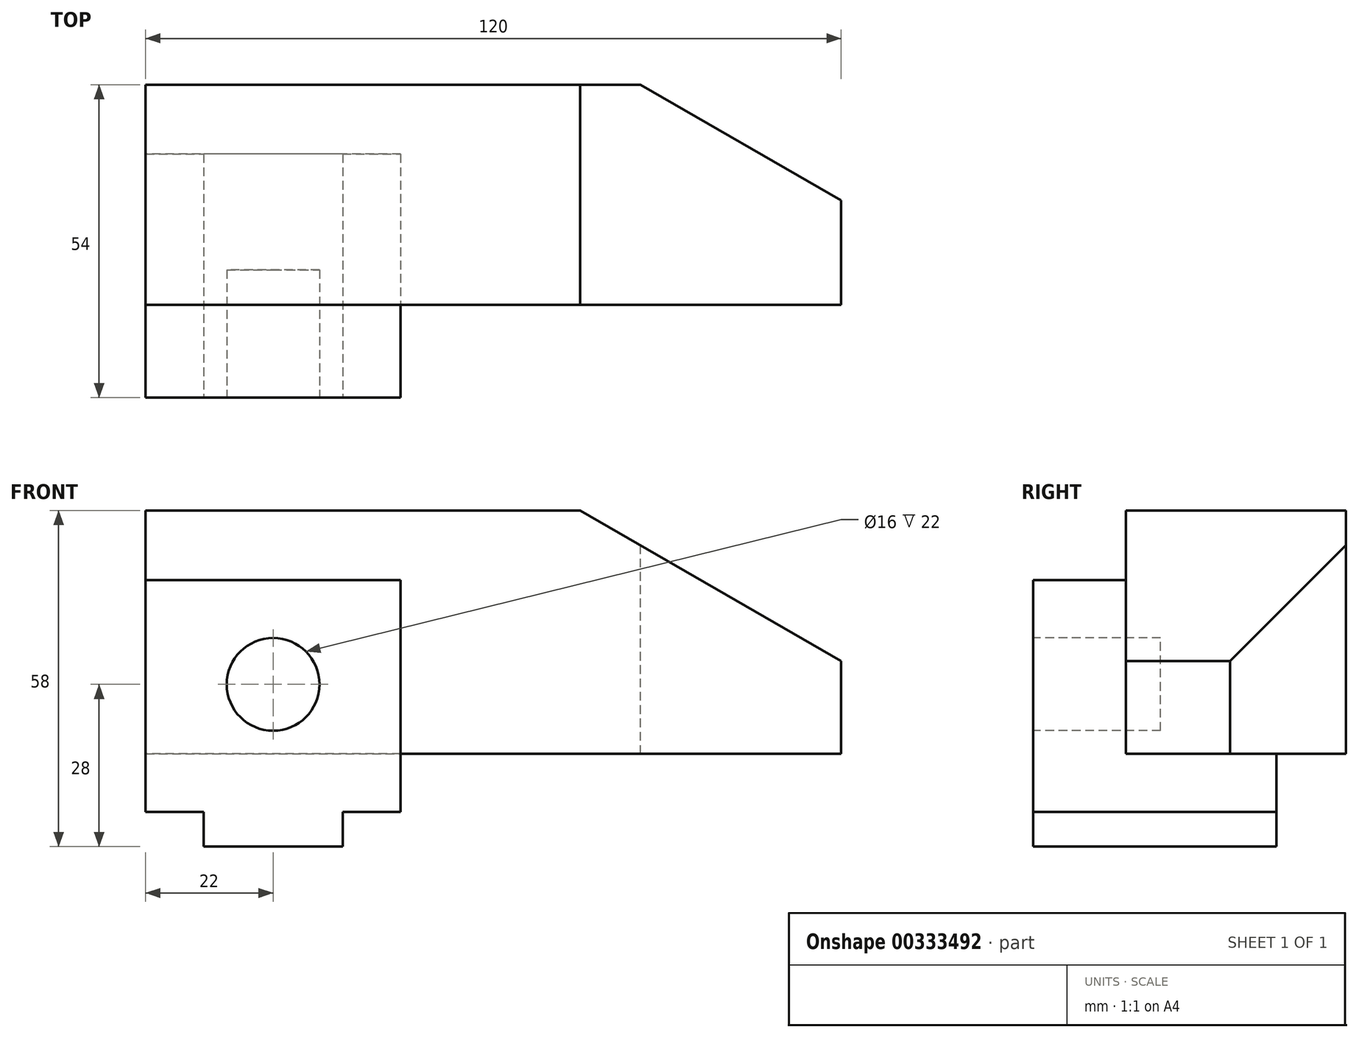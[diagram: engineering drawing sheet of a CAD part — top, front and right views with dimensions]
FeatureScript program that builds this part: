
annotation { "Feature Type Name" : "Feature", "Feature Type Description" : "" }
export const myFeature = defineFeature(function(context is Context, id is Id, definition is map)
    precondition{}
    {
        {
            var Q0;
            Q0=qCreatedBy(makeId("Front.planeOp"),FACE);
            var sketch = newSketch(context, id + "F0", { "sketchPlane" : qUnion([Q0])});
            skLineSegment(sketch, "E0.bottom", {"start": v(0, 0) * mm, "end": v(120, 0) * mm});
            skLineSegment(sketch, "E0.top", {"start": v(0, 58) * mm, "end": v(120, 58) * mm});
            skLineSegment(sketch, "E0.left", {"start": v(0, 0) * mm, "end": v(0, 58) * mm});
            skLineSegment(sketch, "E0.right", {"start": v(120, 0) * mm, "end": v(120, 58) * mm});
            skSolve(sketch);
        }
        {
            var Q0;
            Q0 = qSketchRegion(id + "F0", true);
            extrude(context, id + "F1", {"entities" : qUnion([Q0]), "depth" : 54 * mm});
        }
        {
            var Q0;
            Q0=makeQuery(id+"F1.opExtrude","CAP_FACE",FACE,{"disambiguationData":[OSD([sQuery(id+"F0.wireOp",EDGE,"E0.bottom"),sQuery(id+"F0.wireOp",EDGE,"E0.top"),sQuery(id+"F0.wireOp",EDGE,"E0.left"),sQuery(id+"F0.wireOp",EDGE,"E0.right")])],"isStart":false});
            var sketch = newSketch(context, id + "F2", { "sketchPlane" : qUnion([Q0])});
            skLineSegment(sketch, "E1", {"start": v(34, 0) * mm, "end": v(34, 6) * mm});
            skLineSegment(sketch, "E2", {"start": v(34, 6) * mm, "end": v(44, 6) * mm});
            skLineSegment(sketch, "E3", {"start": v(44, 6) * mm, "end": v(44, 16) * mm});
            skLineSegment(sketch, "E4", {"start": v(44, 16) * mm, "end": v(120, 16) * mm});
            skLineSegment(sketch, "E5", {"start": v(120, 16) * mm, "end": v(120, 0) * mm});
            skLineSegment(sketch, "E6", {"start": v(120, 0) * mm, "end": v(34, 0) * mm});
            skLineSegment(sketch, "E7", {"start": v(75, 58) * mm, "end": v(120, 32.02) * mm});
            skLineSegment(sketch, "E8", {"start": v(120, 32.02) * mm, "end": v(120, 58) * mm});
            skLineSegment(sketch, "E9", {"start": v(120, 58) * mm, "end": v(75, 58) * mm});
            skLineSegment(sketch, "E10.bottom", {"start": v(0, 0) * mm, "end": v(10, 0) * mm});
            skLineSegment(sketch, "E10.top", {"start": v(0, 6) * mm, "end": v(10, 6) * mm});
            skLineSegment(sketch, "E10.left", {"start": v(0, 0) * mm, "end": v(0, 6) * mm});
            skLineSegment(sketch, "E10.right", {"start": v(10, 0) * mm, "end": v(10, 6) * mm});
            skSolve(sketch);
        }
        {
            var Q0;
            Q0 = qSketchRegion(id + "F2", true);
            extrude(context, id + "F3", {"entities" : qUnion([Q0]), "operationType" : NewBodyOperationType.REMOVE, "endBound" : BoundingType.THROUGH_ALL, "oppositeDirection" : true, "depth" : 25 * mm});
        }
        {
            var Q0;
            Q0=makeQuery(id+"F1.opExtrude","CAP_FACE",FACE,{"disambiguationData":[OSD([sQuery(id+"F0.wireOp",EDGE,"E0.bottom"),sQuery(id+"F0.wireOp",EDGE,"E0.top"),sQuery(id+"F0.wireOp",EDGE,"E0.left"),sQuery(id+"F0.wireOp",EDGE,"E0.right")])],"isStart":false});
            var sketch = newSketch(context, id + "F4", { "sketchPlane" : qUnion([Q0])});
            skLineSegment(sketch, "E11", {"start": v(0, 58) * mm, "end": v(0, 46) * mm});
            skLineSegment(sketch, "E12", {"start": v(0, 46) * mm, "end": v(44, 46) * mm});
            skLineSegment(sketch, "E13", {"start": v(44, 46) * mm, "end": v(44, 16) * mm});
            skLineSegment(sketch, "E14", {"start": v(44, 16) * mm, "end": v(120, 16) * mm});
            skLineSegment(sketch, "E15", {"start": v(120, 16) * mm, "end": v(120, 32.02) * mm});
            skLineSegment(sketch, "E16", {"start": v(120, 32.02) * mm, "end": v(75, 58) * mm});
            skLineSegment(sketch, "E17", {"start": v(75, 58) * mm, "end": v(0, 58) * mm});
            skSolve(sketch);
        }
        {
            var Q0;
            Q0 = qSketchRegion(id + "F4", true);
            extrude(context, id + "F5", {"entities" : qUnion([Q0]), "operationType" : NewBodyOperationType.REMOVE, "oppositeDirection" : true, "depth" : 16 * mm});
        }
        {
            var Q0;
            Q0=makeQuery(id+"F1.opExtrude","CAP_FACE",FACE,{"disambiguationData":[OSD([sQuery(id+"F0.wireOp",EDGE,"E0.bottom"),sQuery(id+"F0.wireOp",EDGE,"E0.top"),sQuery(id+"F0.wireOp",EDGE,"E0.left"),sQuery(id+"F0.wireOp",EDGE,"E0.right")])],"isStart":false});
            var sketch = newSketch(context, id + "F6", { "sketchPlane" : qUnion([Q0])});
            skCircle(sketch, "E18", {"center": v(22, 28) * mm, "radius": 8 * mm});
            skPoint(sketch, "E19", {"position": v(39, 6) * mm});
            skSolve(sketch);
        }
        {
            var Q0;
            Q0 = qSketchRegion(id + "F6", true);
            extrude(context, id + "F7", {"entities" : qUnion([Q0]), "operationType" : NewBodyOperationType.REMOVE, "oppositeDirection" : true, "depth" : 22 * mm});
        }
        {
            var Q0;
            Q0=makeQuery(id+"F1.opExtrude","CAP_FACE",FACE,{"disambiguationData":[OSD([sQuery(id+"F0.wireOp",EDGE,"E0.bottom"),sQuery(id+"F0.wireOp",EDGE,"E0.top"),sQuery(id+"F0.wireOp",EDGE,"E0.left"),sQuery(id+"F0.wireOp",EDGE,"E0.right")])],"isStart":true});
            var sketch = newSketch(context, id + "F8", { "sketchPlane" : qUnion([Q0])});
            skLineSegment(sketch, "E20.bottom", {"start": v(-44, 16) * mm, "end": v(0, 16) * mm});
            skLineSegment(sketch, "E20.top", {"start": v(-44, 0) * mm, "end": v(0, 0) * mm});
            skLineSegment(sketch, "E20.left", {"start": v(-44, 16) * mm, "end": v(-44, 0) * mm});
            skLineSegment(sketch, "E20.right", {"start": v(0, 16) * mm, "end": v(0, 0) * mm});
            skSolve(sketch);
        }
        {
            var Q0;
            Q0 = qSketchRegion(id + "F8", true);
            extrude(context, id + "F9", {"entities" : qUnion([Q0]), "operationType" : NewBodyOperationType.REMOVE, "oppositeDirection" : true, "depth" : 12 * mm});
        }
        {
            var Q0;
            Q0=makeQuery(id+"F1.opExtrude","SWEPT_FACE",FACE,{"disambiguationData":[OSD([sQuery(id+"F0.wireOp",EDGE,"E0.top")])]});
            var sketch = newSketch(context, id + "F10", { "sketchPlane" : qUnion([Q0])});
            skLineSegment(sketch, "E21.0.2", {"start": v(120, -20) * mm, "end": v(120, 0) * mm});
            skLineSegment(sketch, "E21.0.3", {"start": v(120, 0) * mm, "end": v(85.36, 0) * mm});
            skLineSegment(sketch, "E22", {"start": v(120, -20) * mm, "end": v(85.36, 0) * mm});
            skPoint(sketch, "E21.0.0.start.orphan", {"position": v(75, 0) * mm});
            skPoint(sketch, "E21.0.1.start.orphan", {"position": v(75, -38) * mm});
            skPoint(sketch, "E23.orphan", {"position": v(120, -38) * mm});
            skSolve(sketch);
        }
        {
            var Q0;
            Q0 = qSketchRegion(id + "F10", true);
            extrude(context, id + "F11", {"entities" : qUnion([Q0]), "operationType" : NewBodyOperationType.REMOVE, "endBound" : BoundingType.THROUGH_ALL, "oppositeDirection" : true, "depth" : 25 * mm});
        }
    });
